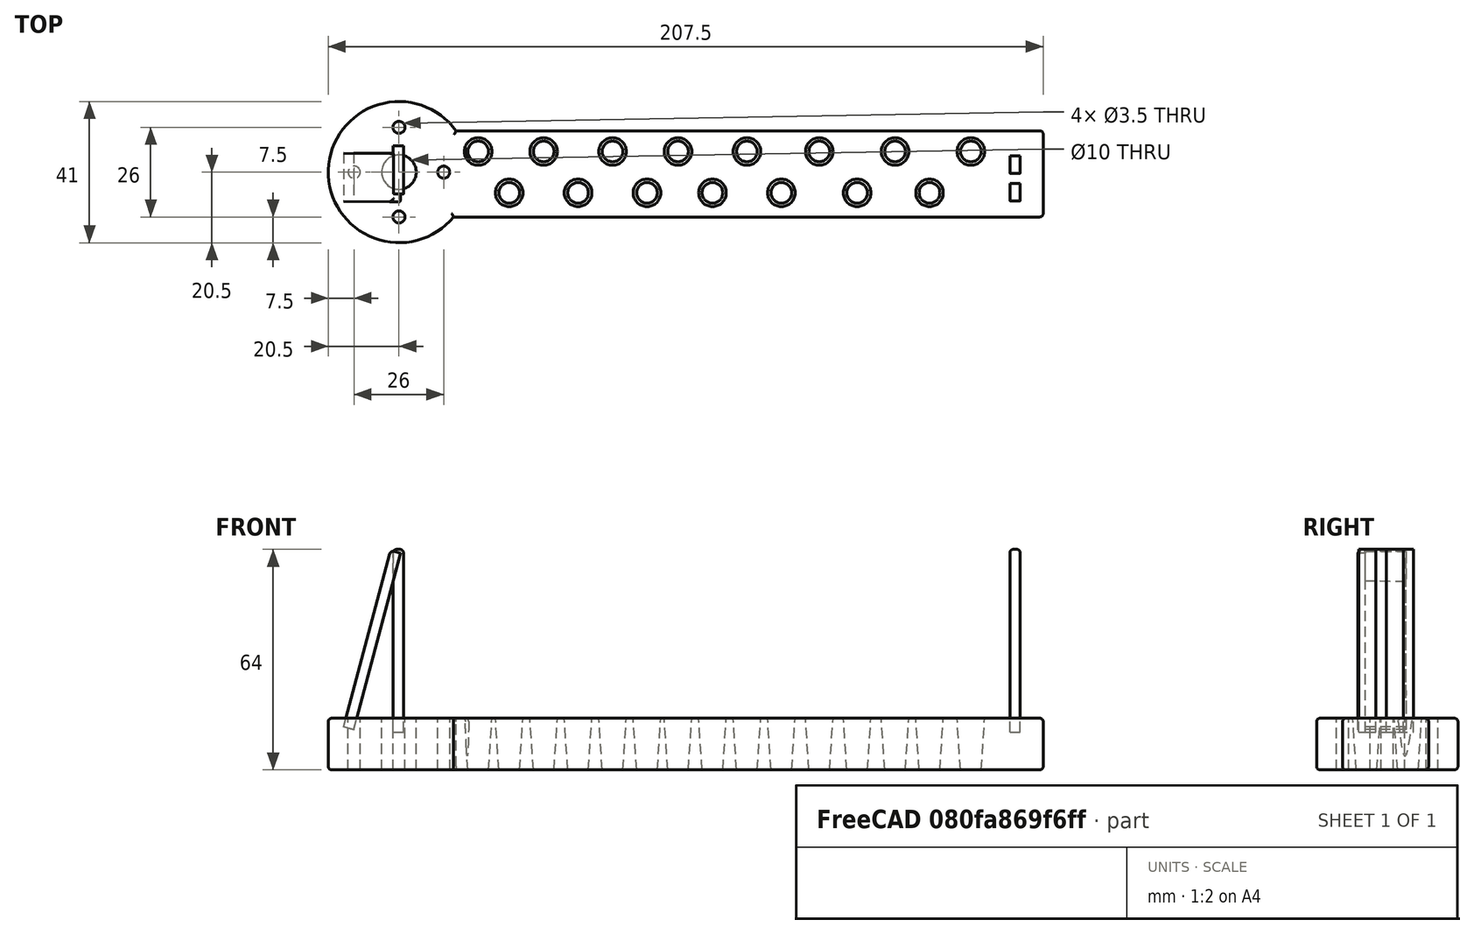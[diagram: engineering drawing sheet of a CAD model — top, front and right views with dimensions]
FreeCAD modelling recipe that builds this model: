
FCSTD DOCUMENT  (FreeCAD 0.18R16117 (Git))
Label: asd
License: All rights reserved
LicenseURL: http://en.wikipedia.org/wiki/All_rights_reserved
objects: Part::Cut×20, Part::Cone×15, Part::Fillet×7, Part::Cylinder×6, Part::Box×5, Part::MultiFuse×2
note: 55 computed .brp shape members not serialized (recipe doc carries the construction recipe); baked Part::Feature solids carry a one-line shape summary decoded from their .brp

FEATURE [Part::Box] Box  label="Cube"
  AttacherType = Attacher::AttachEngine3D
  Height = 15
  Length = 172
  Width = 25
FEATURE [Part::Box] Box001  label="Cube001"
  AttacherType = Attacher::AttachEngine3D
  Height = 14
  Length = 53
  Placement = pos=(-28.1211,18.5263,11.6767) rot=(-0.676931,0.521894,-0.519029;4.3325rad)
  Width = 3
FEATURE [Part::Cylinder] Cylinder
  Angle = 360
  AttacherType = Attacher::AttachEngine3D
  Height = 15
  Placement = pos=(47,75,0) rot=(0,0,1;0rad)
  Radius = 5
FEATURE [Part::Box] Box002  label="Cube002"
  AttacherType = Attacher::AttachEngine3D
  Height = 14
  Length = 53
  Placement = pos=(-16.68,6.66963,11) rot=(0.57735,0.57735,0.57735;4.18879rad)
  Width = 3
FEATURE [Part::Fillet] Fillet001
  Base = -> Box
  Edges = 4 edges r=1: [Edge9,Edge10,Edge11,Edge12]
FEATURE [Part::Cylinder] Cylinder004
  Angle = 360
  AttacherType = Attacher::AttachEngine3D
  Height = 15
  Placement = pos=(34,75,0) rot=(0,0,1;0rad)
  Radius = 1.75
FEATURE [Part::Cylinder] Cylinder005
  Angle = 360
  AttacherType = Attacher::AttachEngine3D
  Height = 15
  Placement = pos=(47,75,0) rot=(0,0,1;0rad)
  Radius = 20.5
FEATURE [Part::Cut] Cut
  Base = -> Cylinder005
  Tool = -> Cylinder
FEATURE [Part::Cylinder] Cylinder006
  Angle = 360
  AttacherType = Attacher::AttachEngine3D
  Height = 15
  Placement = pos=(60,75,0) rot=(0,0,1;0rad)
  Radius = 1.75
FEATURE [Part::Cylinder] Cylinder007
  Angle = 360
  AttacherType = Attacher::AttachEngine3D
  Height = 15
  Placement = pos=(47,88,0) rot=(0,0,1;0rad)
  Radius = 1.75
FEATURE [Part::Cylinder] Cylinder008
  Angle = 360
  AttacherType = Attacher::AttachEngine3D
  Height = 15
  Placement = pos=(47,62,0) rot=(0,0,1;0rad)
  Radius = 1.75
FEATURE [Part::Cut] Cut001
  Base = -> Cut
  Tool = -> Cylinder007
FEATURE [Part::Cut] Cut002
  Base = -> Cut001
  Tool = -> Cylinder006
FEATURE [Part::Cut] Cut003
  Base = -> Cut002
  Tool = -> Cylinder004
FEATURE [Part::Cut] Cut004
  Base = -> Cut003
  Tool = -> Cylinder008
FEATURE [Part::Fillet] Fillet
  Base = -> Cut004
  Edges = 2 edges r=1: [Edge1,Edge3]
  Placement = pos=(-62,-62,0) rot=(0,0,1;0rad)
FEATURE [Part::Fillet] Fillet002
  Base = -> Box002
  Edges = 2 edges r=1: [Edge5,Edge7]
FEATURE [Part::Fillet] Fillet003
  Base = -> Box001
  Edges = 2 edges r=1: [Edge6,Edge7]
FEATURE [Part::Box] Box003  label="Cube003"
  AttacherType = Attacher::AttachEngine3D
  Height = 5
  Length = 53
  Placement = pos=(-15.68,12.67,11) rot=(0.57735,0.57735,0.57735;4.18879rad)
  Width = 3
FEATURE [Part::Fillet] Fillet004
  Base = -> Box003
  Edges = 2 edges r=1: [Edge5,Edge7]
  Placement = pos=(178,0,0) rot=(0,0,1;0rad)
FEATURE [Part::Box] Box004  label="Cube004"
  AttacherType = Attacher::AttachEngine3D
  Height = 5
  Length = 53
  Placement = pos=(-15.68,12.67,11) rot=(0.57735,0.57735,0.57735;4.18879rad)
  Width = 3
FEATURE [Part::Fillet] Fillet005
  Base = -> Box004
  Edges = 2 edges r=1: [Edge5,Edge7]
  Placement = pos=(178,-8,0) rot=(0,0,1;0rad)
FEATURE [Part::Cone] Cone
  Angle = 360
  AttacherType = Attacher::AttachEngine3D
  Height = 30
  Placement = pos=(151,19,-15) rot=(0,0,1;0rad)
  Radius1 = 2
  Radius2 = 4
FEATURE [Part::Cone] Cone001
  Angle = 360
  AttacherType = Attacher::AttachEngine3D
  Height = 30
  Placement = pos=(139,7,-15) rot=(0,0,1;0rad)
  Radius1 = 2
  Radius2 = 4
FEATURE [Part::Cone] Cone002
  Angle = 360
  AttacherType = Attacher::AttachEngine3D
  Height = 30
  Placement = pos=(129,19,-15) rot=(0,0,1;0rad)
  Radius1 = 2
  Radius2 = 4
FEATURE [Part::Cut] Cut005
  Base = -> Fillet001
  Tool = -> Cone
FEATURE [Part::Fillet] Fillet006
  Base = -> Cut005
  Edges = 4 edges r=1: [Edge9,Edge17,Edge20,Edge26]
FEATURE [Part::Cone] Cone003
  Angle = 360
  AttacherType = Attacher::AttachEngine3D
  Height = 30
  Placement = pos=(118,7,-15) rot=(0,0,1;0rad)
  Radius1 = 2
  Radius2 = 4
FEATURE [Part::Cone] Cone004
  Angle = 360
  AttacherType = Attacher::AttachEngine3D
  Height = 30
  Placement = pos=(107,19,-15) rot=(0,0,1;0rad)
  Radius1 = 2
  Radius2 = 4
FEATURE [Part::Cone] Cone005
  Angle = 360
  AttacherType = Attacher::AttachEngine3D
  Height = 30
  Placement = pos=(86,19,-15) rot=(0,0,1;0rad)
  Radius1 = 2
  Radius2 = 4
FEATURE [Part::Cone] Cone006
  Angle = 360
  AttacherType = Attacher::AttachEngine3D
  Height = 30
  Placement = pos=(66,19,-15) rot=(0,0,1;0rad)
  Radius1 = 2
  Radius2 = 4
FEATURE [Part::Cone] Cone007
  Angle = 360
  AttacherType = Attacher::AttachEngine3D
  Height = 30
  Placement = pos=(47,19,-15) rot=(0,0,1;0rad)
  Radius1 = 2
  Radius2 = 4
FEATURE [Part::Cone] Cone008
  Angle = 360
  AttacherType = Attacher::AttachEngine3D
  Height = 30
  Placement = pos=(27,19,-15) rot=(0,0,1;0rad)
  Radius1 = 2
  Radius2 = 4
FEATURE [Part::Cone] Cone009
  Angle = 360
  AttacherType = Attacher::AttachEngine3D
  Height = 30
  Placement = pos=(8,19,-15) rot=(0,0,1;0rad)
  Radius1 = 2
  Radius2 = 4
FEATURE [Part::Cone] Cone010
  Angle = 360
  AttacherType = Attacher::AttachEngine3D
  Height = 30
  Placement = pos=(96,7,-15) rot=(0,0,1;0rad)
  Radius1 = 2
  Radius2 = 4
FEATURE [Part::Cone] Cone011
  Angle = 360
  AttacherType = Attacher::AttachEngine3D
  Height = 30
  Placement = pos=(76,7,-15) rot=(0,0,1;0rad)
  Radius1 = 2
  Radius2 = 4
FEATURE [Part::Cone] Cone012
  Angle = 360
  AttacherType = Attacher::AttachEngine3D
  Height = 30
  Placement = pos=(57,7,-15) rot=(0,0,1;0rad)
  Radius1 = 2
  Radius2 = 4
FEATURE [Part::Cone] Cone013
  Angle = 360
  AttacherType = Attacher::AttachEngine3D
  Height = 30
  Placement = pos=(37,7,-15) rot=(0,0,1;0rad)
  Radius1 = 2
  Radius2 = 4
FEATURE [Part::Cone] Cone014
  Angle = 360
  AttacherType = Attacher::AttachEngine3D
  Height = 30
  Placement = pos=(17,7,-15) rot=(0,0,1;0rad)
  Radius1 = 2
  Radius2 = 4
FEATURE [Part::Cut] Cut006
  Base = -> Fillet006
  Tool = -> Cone001
FEATURE [Part::Cut] Cut007
  Base = -> Cut006
  Tool = -> Cone010
FEATURE [Part::Cut] Cut008
  Base = -> Cut007
  Tool = -> Cone014
FEATURE [Part::Cut] Cut009
  Base = -> Cut008
  Tool = -> Cone013
FEATURE [Part::Cut] Cut010
  Base = -> Cut009
  Tool = -> Cone012
FEATURE [Part::Cut] Cut011
  Base = -> Cut010
  Tool = -> Cone011
FEATURE [Part::Cut] Cut012
  Base = -> Cut011
  Tool = -> Cone008
FEATURE [Part::Cut] Cut013
  Base = -> Cut012
  Tool = -> Cone009
FEATURE [Part::Cut] Cut014
  Base = -> Cut013
  Tool = -> Cone007
FEATURE [Part::Cut] Cut015
  Base = -> Cut014
  Tool = -> Cone006
FEATURE [Part::Cut] Cut016
  Base = -> Cut015
  Tool = -> Cone005
FEATURE [Part::Cut] Cut017
  Base = -> Cut016
  Tool = -> Cone004
FEATURE [Part::Cut] Cut018
  Base = -> Cut017
  Tool = -> Cone003
FEATURE [Part::Cut] Cut019
  Base = -> Cut018
  Tool = -> Cone002
FEATURE [Part::MultiFuse] Fusion  label="Legs"
  Shapes = -> [Fillet002,Fillet003,Fillet004,Fillet005]
FEATURE [Part::MultiFuse] Fusion001  label="Top"
  Shapes = -> [Cut019,Fillet]
